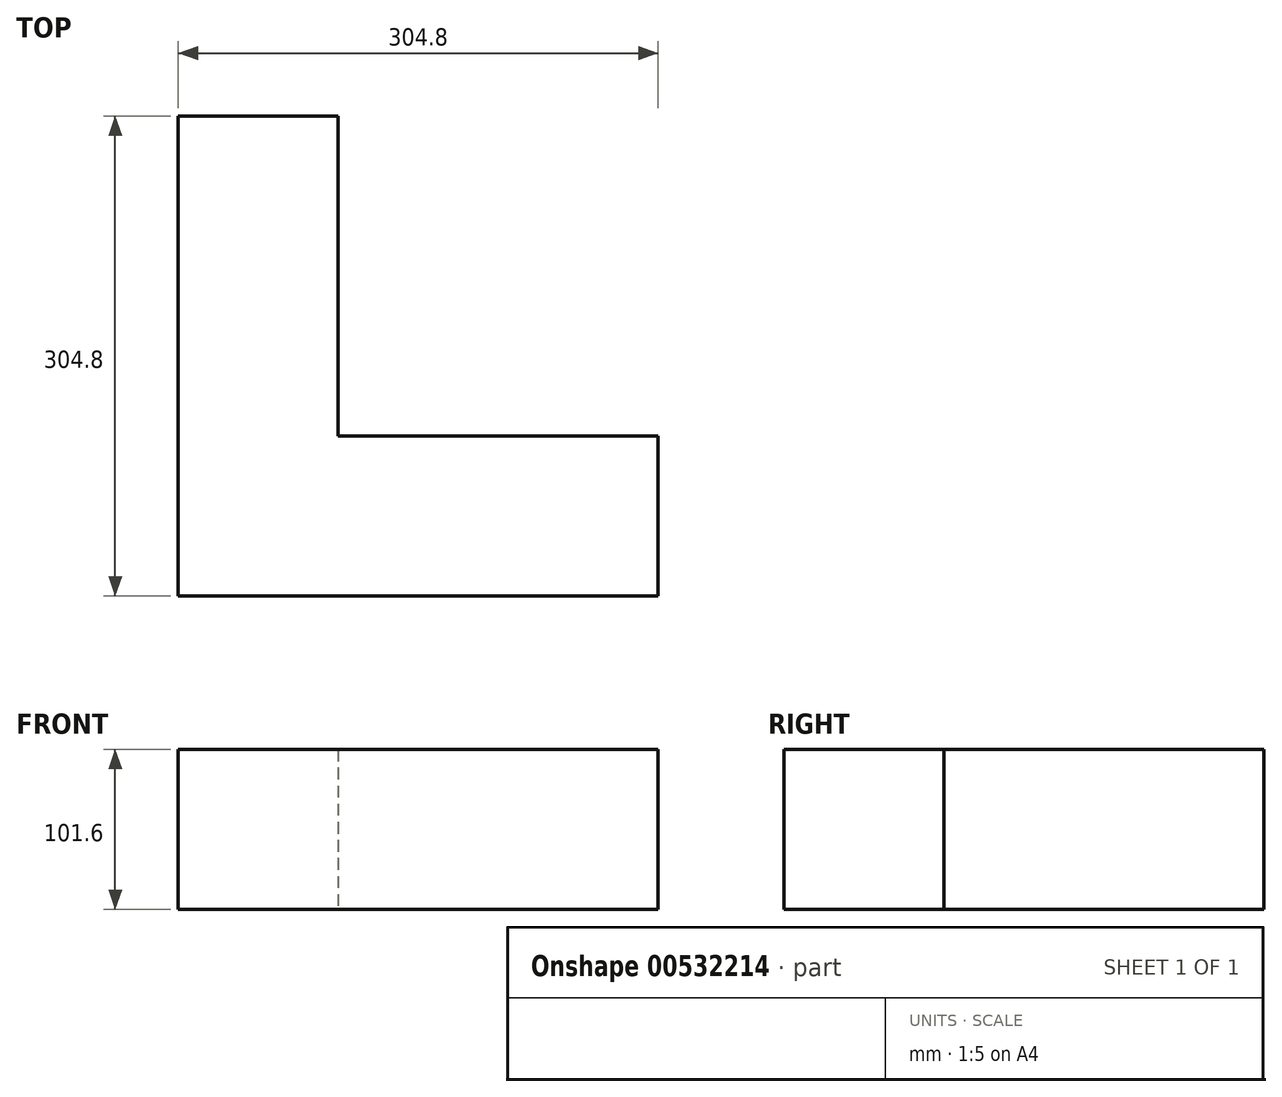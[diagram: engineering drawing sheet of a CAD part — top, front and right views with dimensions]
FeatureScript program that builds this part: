
annotation { "Feature Type Name" : "Feature", "Feature Type Description" : "" }
export const myFeature = defineFeature(function(context is Context, id is Id, definition is map)
    precondition{}
    {
        {
            var Q0;
            Q0=qCreatedBy(makeId("Top.planeOp"),FACE);
            var sketch = newSketch(context, id + "F0", { "sketchPlane" : qUnion([Q0])});
            skLineSegment(sketch, "E0", {"start": v(0, 0) * mm, "end": v(0, 203.2) * mm});
            skLineSegment(sketch, "E1", {"start": v(0, 203.2) * mm, "end": v(-101.6, 203.2) * mm});
            skLineSegment(sketch, "E2", {"start": v(-101.6, 203.2) * mm, "end": v(-101.6, -101.6) * mm});
            skLineSegment(sketch, "E3", {"start": v(-101.6, -101.6) * mm, "end": v(203.2, -101.6) * mm});
            skLineSegment(sketch, "E4", {"start": v(203.2, -101.6) * mm, "end": v(203.2, 0) * mm});
            skLineSegment(sketch, "E5", {"start": v(203.2, 0) * mm, "end": v(0, 0) * mm});
            skSolve(sketch);
        }
        {
            var Q0;
            Q0=makeQuery(id+"F0.imprint","IMPRINT",FACE,{"disambiguationData":[TD([[makeQuery(id+"F0.imprint","IMPRINT",EDGE,{"derivedFrom":sQuery(id+"F0.wireOp",EDGE,"E0")}),1.0]])]});
            extrude(context, id + "F1", {"entities" : qUnion([Q0]), "depth" : 101.6 * mm, "offsetDistance" : 25.4 * mm});
        }
    });
